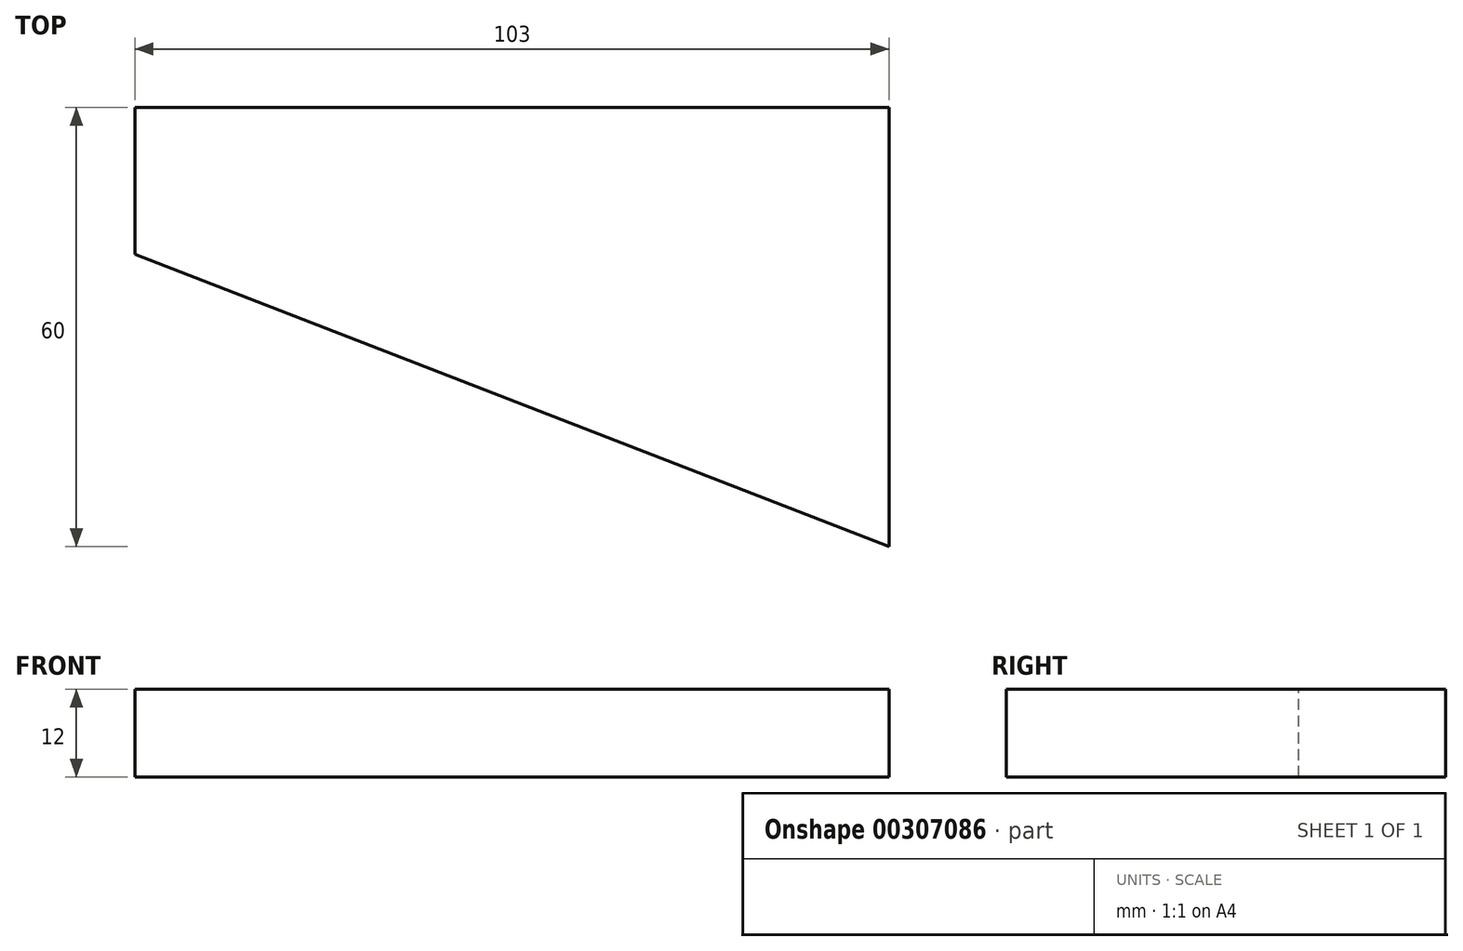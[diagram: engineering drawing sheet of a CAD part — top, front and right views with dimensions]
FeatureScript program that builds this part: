
annotation { "Feature Type Name" : "Feature", "Feature Type Description" : "" }
export const myFeature = defineFeature(function(context is Context, id is Id, definition is map)
    precondition{}
    {
        {
            var Q0;
            Q0=qCreatedBy(makeId("Front.planeOp"),FACE);
            var sketch = newSketch(context, id + "F0", { "sketchPlane" : qUnion([Q0])});
            skLineSegment(sketch, "E0.bottom", {"start": v(-38, 1.13) * mm, "end": v(65, 1.13) * mm});
            skLineSegment(sketch, "E0.top", {"start": v(-38, -10.87) * mm, "end": v(65, -10.87) * mm});
            skLineSegment(sketch, "E0.left", {"start": v(-38, 1.13) * mm, "end": v(-38, -10.87) * mm});
            skLineSegment(sketch, "E0.right", {"start": v(65, 1.13) * mm, "end": v(65, -10.87) * mm});
            skSolve(sketch);
        }
        {
            var Q0;
            Q0=makeQuery(id+"F0.imprint","IMPRINT",FACE,{"disambiguationData":[TD([[makeQuery(id+"F0.imprint","IMPRINT",EDGE,{"derivedFrom":sQuery(id+"F0.wireOp",EDGE,"E0.bottom")}),-1.0]])]});
            extrude(context, id + "F1", {"entities" : qUnion([Q0]), "depth" : 60 * mm});
        }
        {
            var Q0;
            Q0=makeQuery(id+"F1.opExtrude","SWEPT_FACE",FACE,{"disambiguationData":[OSD([sQuery(id+"F0.wireOp",EDGE,"E0.bottom")])]});
            var sketch = newSketch(context, id + "F2", { "sketchPlane" : qUnion([Q0])});
            skLineSegment(sketch, "E1", {"start": v(-38, 0) * mm, "end": v(-38, -20.04) * mm});
            skLineSegment(sketch, "E2", {"start": v(-38, -20.04) * mm, "end": v(65, -60) * mm});
            skSolve(sketch);
        }
        {
            var Q0;
            {var subQ0=sQuery(id+"F2.wireOp",EDGE,"E2");Q0=makeQuery(id+"F2.imprint","IMPRINT",FACE,{"disambiguationData":[TD([[makeQuery(id+"F2.imprint","IMPRINT",EDGE,{"derivedFrom":subQ0}),-1.0]])]});}
            extrude(context, id + "F3", {"entities" : qUnion([Q0]), "operationType" : NewBodyOperationType.REMOVE, "oppositeDirection" : true, "depth" : 12 * mm});
        }
    });
